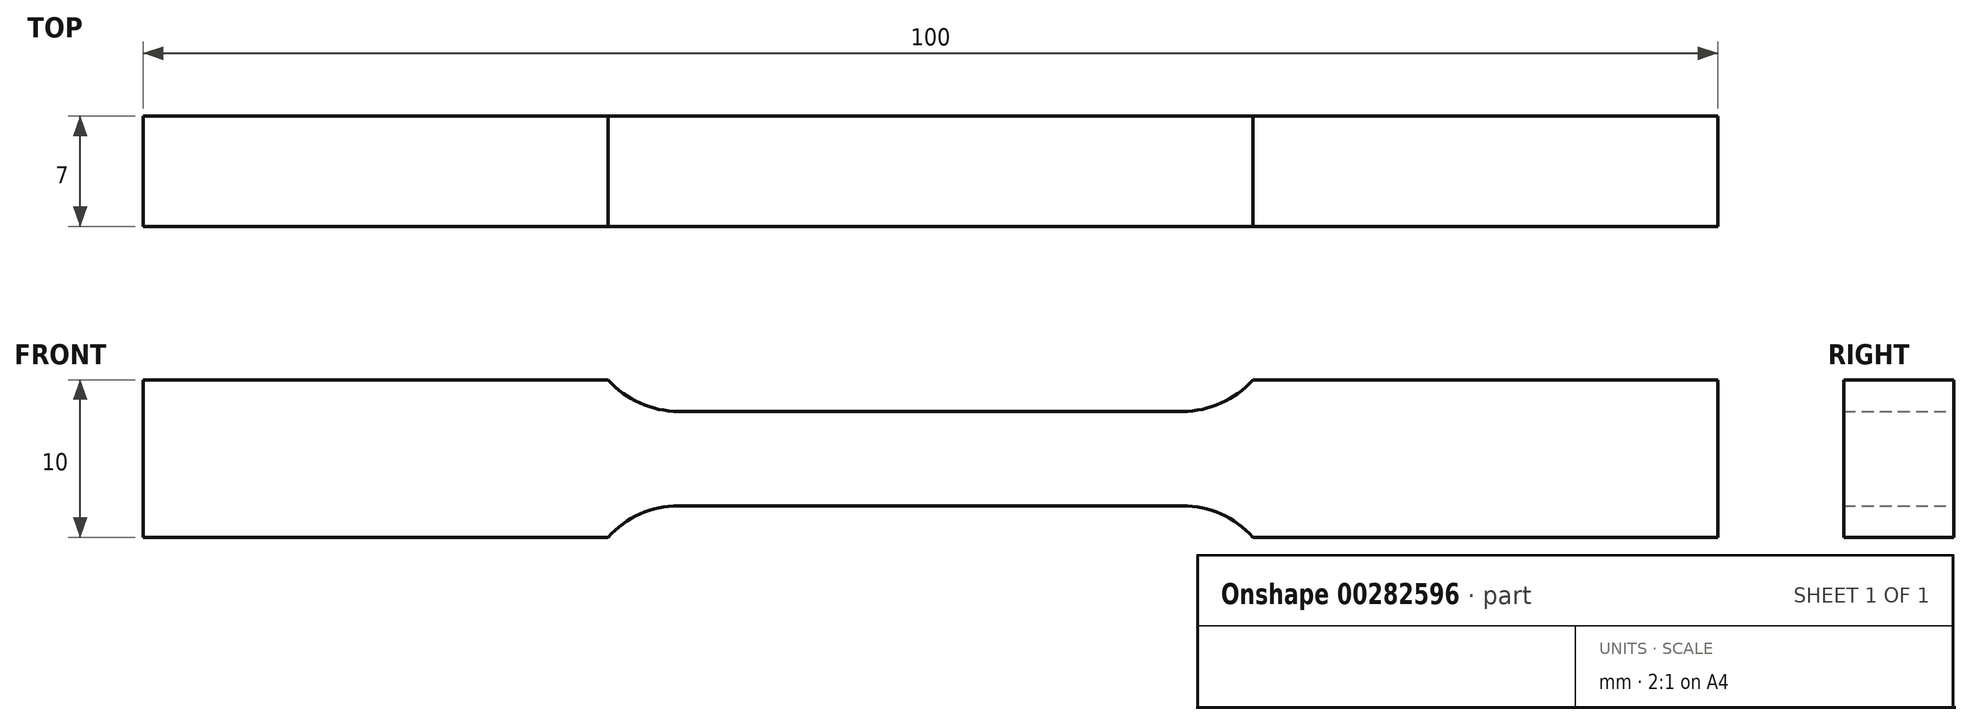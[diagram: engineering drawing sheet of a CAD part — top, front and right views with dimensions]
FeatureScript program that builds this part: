
annotation { "Feature Type Name" : "Feature", "Feature Type Description" : "" }
export const myFeature = defineFeature(function(context is Context, id is Id, definition is map)
    precondition{}
    {
        {
            var Q0;
            Q0=qCreatedBy(makeId("Front.planeOp"),FACE);
            var sketch = newSketch(context, id + "F0", { "sketchPlane" : qUnion([Q0])});
            skLineSegment(sketch, "E0", {"start": v(0, 3) * mm, "end": v(16, 3) * mm});
            skArc(sketch, "E1", {"start": v(16, 3) * mm, "mid": v(18.45, 3.52) * mm, "end": v(20.47, 5) * mm});
            skLineSegment(sketch, "E2", {"start": v(20.47, 5) * mm, "end": v(50, 5) * mm});
            skLineSegment(sketch, "E3.MirrorCS", {"start": v(0, -3) * mm, "end": v(16, -3) * mm});
            skLineSegment(sketch, "E4.MirrorCS", {"start": v(20.47, -5) * mm, "end": v(50, -5) * mm});
            skArc(sketch, "E5.MirrorCS", {"start": v(16, -3) * mm, "mid": v(18.45, -3.52) * mm, "end": v(20.47, -5) * mm});
            skLineSegment(sketch, "E6", {"start": v(50, 5) * mm, "end": v(50, -5) * mm});
            skLineSegment(sketch, "E7.MirrorCS", {"start": v(0, 3) * mm, "end": v(-16, 3) * mm});
            skArc(sketch, "E8.MirrorCS", {"start": v(-16, 3) * mm, "mid": v(-18.45, 3.52) * mm, "end": v(-20.47, 5) * mm});
            skLineSegment(sketch, "E9.MirrorCS", {"start": v(-20.47, 5) * mm, "end": v(-50, 5) * mm});
            skLineSegment(sketch, "E10.MirrorCS", {"start": v(0, -3) * mm, "end": v(-16, -3) * mm});
            skLineSegment(sketch, "E11.MirrorCS", {"start": v(-20.47, -5) * mm, "end": v(-50, -5) * mm});
            skLineSegment(sketch, "E12.MirrorCS", {"start": v(-50, 5) * mm, "end": v(-50, -5) * mm});
            skArc(sketch, "E13.MirrorCS", {"start": v(-16, -3) * mm, "mid": v(-18.45, -3.52) * mm, "end": v(-20.47, -5) * mm});
            skSolve(sketch);
        }
        {
            var Q0;
            Q0=makeQuery(id+"F0.imprint","IMPRINT",FACE,{"disambiguationData":[TD([[makeQuery(id+"F0.imprint","IMPRINT",EDGE,{"derivedFrom":sQuery(id+"F0.wireOp",EDGE,"E0")}),-1.0]])]});
            extrude(context, id + "F1", {"entities" : qUnion([Q0]), "endBound" : BoundingType.SYMMETRIC, "depth" : 7 * mm});
        }
    });
